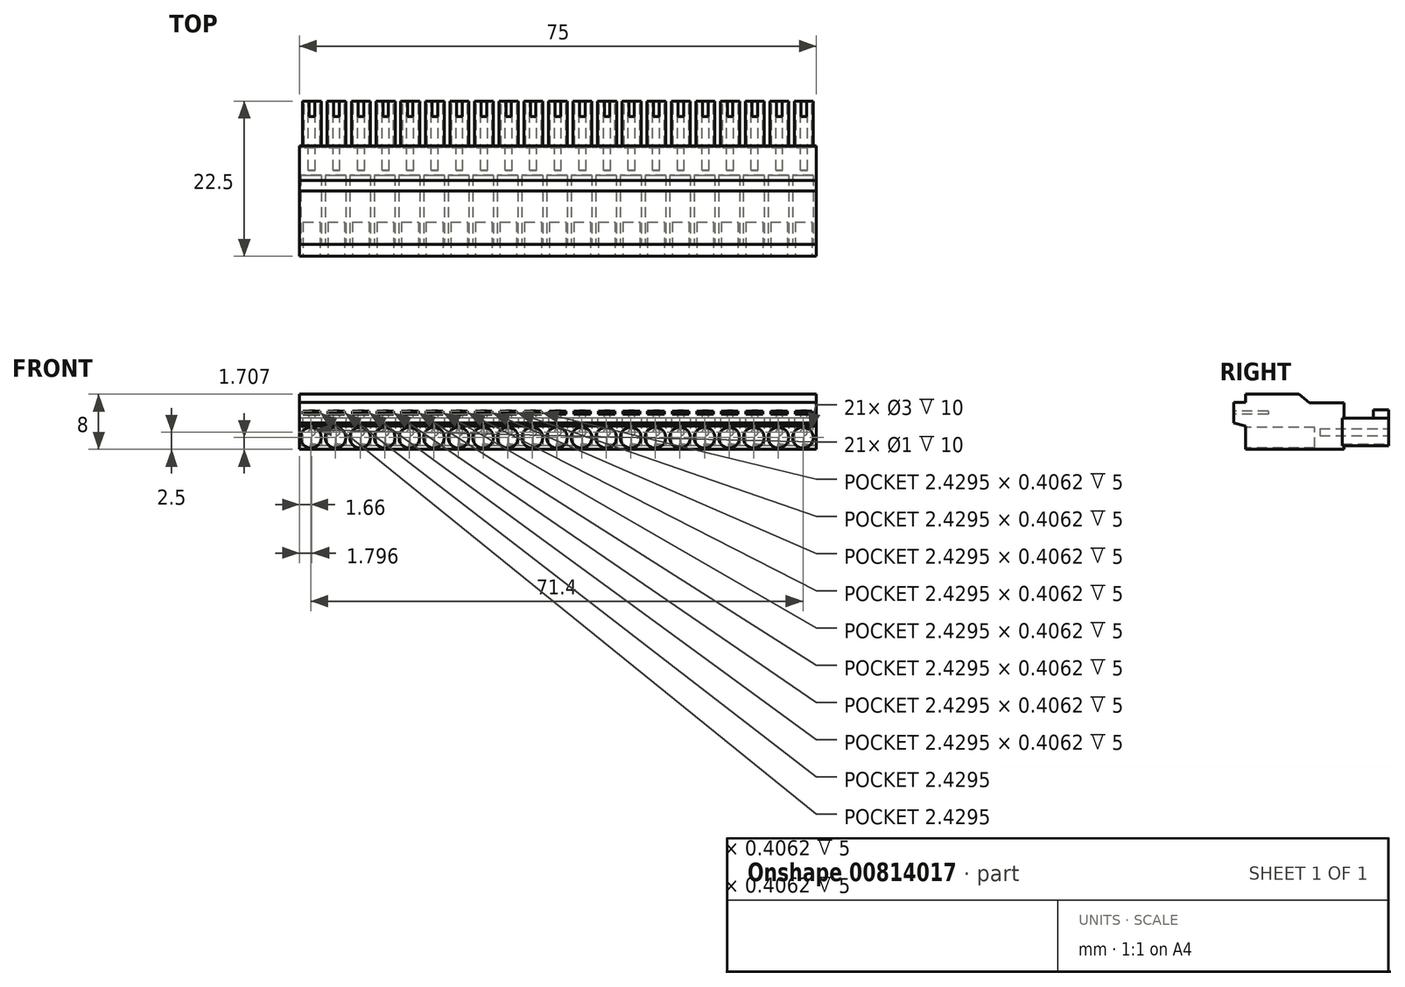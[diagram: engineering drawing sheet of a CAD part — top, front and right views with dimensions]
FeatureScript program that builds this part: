
annotation { "Feature Type Name" : "Feature", "Feature Type Description" : "" }
export const myFeature = defineFeature(function(context is Context, id is Id, definition is map)
    precondition{}
    {
        {
            var Q0;
            Q0=qCreatedBy(makeId("Right.planeOp"),FACE);
            var sketch = newSketch(context, id + "F0", { "sketchPlane" : qUnion([Q0])});
            skLineSegment(sketch, "E0", {"start": v(0, 0) * mm, "end": v(-14.25, 0) * mm});
            skLineSegment(sketch, "E1", {"start": v(-14.25, 0) * mm, "end": v(-14.25, 3.41) * mm});
            skLineSegment(sketch, "E2", {"start": v(-14.25, 8) * mm, "end": v(-6.5, 8) * mm});
            skLineSegment(sketch, "E3", {"start": v(0, 0) * mm, "end": v(0, 6.75) * mm});
            skLineSegment(sketch, "E4", {"start": v(0, 6.75) * mm, "end": v(-5, 6.75) * mm});
            skLineSegment(sketch, "E5", {"start": v(-5, 6.75) * mm, "end": v(-6.5, 8) * mm});
            skPoint(sketch, "E6.orphan", {"position": v(-5, 8) * mm});
            skLineSegment(sketch, "E7", {"start": v(-16, 3.83) * mm, "end": v(-16, 6.83) * mm});
            skLineSegment(sketch, "E8", {"start": v(-16, 6.83) * mm, "end": v(-14.25, 6.83) * mm});
            skLineSegment(sketch, "E9", {"start": v(-16, 3.83) * mm, "end": v(-14.25, 3.41) * mm});
            skLineSegment(sketch, "E10.trimOffspring", {"start": v(-14.25, 6.83) * mm, "end": v(-14.25, 8) * mm});
            skPoint(sketch, "E11.orphan", {"position": v(-14.25, 4) * mm});
            skLineSegment(sketch, "E12", {"start": v(0, 0) * mm, "end": v(0, 0.5) * mm});
            skLineSegment(sketch, "E13", {"start": v(0, 0.5) * mm, "end": v(6.5, 0.5) * mm});
            skLineSegment(sketch, "E14", {"start": v(6.5, 0.5) * mm, "end": v(6.5, 4.5) * mm});
            skLineSegment(sketch, "E15", {"start": v(6.5, 4.5) * mm, "end": v(0, 4.5) * mm});
            skSolve(sketch);
        }
        {
            var Q0;
            Q0=qSketchRegion(id+"F0",true);
            extrude(context, id + "F1", {"entities" : qUnion([Q0]), "depth" : 75 * mm, "offsetDistance" : 25 * mm});
        }
        {
            var Q0;
            Q0=makeQuery(id+"F1.opExtrude","SWEPT_FACE",FACE,{"disambiguationData":[OSD([sQuery(id+"F0.wireOp",EDGE,"E1")])]});
            var sketch = newSketch(context, id + "F2", { "sketchPlane" : qUnion([Q0])});
            skLineSegment(sketch, "E16", {"start": v(0, 1.7) * mm, "end": v(75, 1.7) * mm, "construction": true});
            skCircle(sketch, "E17", {"center": v(1.66, 1.7) * mm, "radius": 1.5 * mm});
            skCircle(sketch, "E18.1.0.0", {"center": v(5.23, 1.7) * mm, "radius": 1.5 * mm});
            skCircle(sketch, "E18.2.0.0", {"center": v(8.8, 1.7) * mm, "radius": 1.5 * mm});
            skCircle(sketch, "E18.3.0.0", {"center": v(12.37, 1.7) * mm, "radius": 1.5 * mm});
            skCircle(sketch, "E18.4.0.0", {"center": v(15.94, 1.7) * mm, "radius": 1.5 * mm});
            skCircle(sketch, "E18.5.0.0", {"center": v(19.51, 1.7) * mm, "radius": 1.5 * mm});
            skCircle(sketch, "E18.6.0.0", {"center": v(23.08, 1.7) * mm, "radius": 1.5 * mm});
            skCircle(sketch, "E18.7.0.0", {"center": v(26.65, 1.7) * mm, "radius": 1.5 * mm});
            skCircle(sketch, "E18.8.0.0", {"center": v(30.22, 1.7) * mm, "radius": 1.5 * mm});
            skCircle(sketch, "E18.9.0.0", {"center": v(33.8, 1.7) * mm, "radius": 1.5 * mm});
            skCircle(sketch, "E18.10.0.0", {"center": v(37.36, 1.7) * mm, "radius": 1.5 * mm});
            skCircle(sketch, "E18.11.0.0", {"center": v(40.93, 1.7) * mm, "radius": 1.5 * mm});
            skCircle(sketch, "E18.12.0.0", {"center": v(44.5, 1.7) * mm, "radius": 1.5 * mm});
            skCircle(sketch, "E18.13.0.0", {"center": v(48.07, 1.7) * mm, "radius": 1.5 * mm});
            skCircle(sketch, "E18.14.0.0", {"center": v(51.64, 1.7) * mm, "radius": 1.5 * mm});
            skCircle(sketch, "E18.15.0.0", {"center": v(55.21, 1.7) * mm, "radius": 1.5 * mm});
            skCircle(sketch, "E18.16.0.0", {"center": v(58.78, 1.7) * mm, "radius": 1.5 * mm});
            skCircle(sketch, "E18.17.0.0", {"center": v(62.35, 1.7) * mm, "radius": 1.5 * mm});
            skCircle(sketch, "E18.18.0.0", {"center": v(65.92, 1.7) * mm, "radius": 1.5 * mm});
            skCircle(sketch, "E18.19.0.0", {"center": v(69.5, 1.7) * mm, "radius": 1.5 * mm});
            skCircle(sketch, "E18.20.0.0", {"center": v(73.06, 1.7) * mm, "radius": 1.5 * mm});
            skLineSegment(sketch, "E18.direction1", {"start": v(1.66, 1.7) * mm, "end": v(5.23, 1.7) * mm, "construction": true});
            skSolve(sketch);
        }
        {
            var Q0;
            Q0=qSketchRegion(id+"F2",true);
            extrude(context, id + "F3", {"entities" : qUnion([Q0]), "operationType" : NewBodyOperationType.REMOVE, "oppositeDirection" : true, "depth" : 10 * mm, "offsetDistance" : 25 * mm});
        }
        {
            var Q0;
            Q0=makeQuery(id+"F1.opExtrude","SWEPT_FACE",FACE,{"disambiguationData":[OSD([sQuery(id+"F0.wireOp",EDGE,"E14")])]});
            var sketch = newSketch(context, id + "F4", { "sketchPlane" : qUnion([Q0])});
            skLineSegment(sketch, "E19", {"start": v(-75, 2.5) * mm, "end": v(0, 2.5) * mm, "construction": true});
            skCircle(sketch, "E20", {"center": v(-73.2, 2.5) * mm, "radius": 0.5 * mm});
            skCircle(sketch, "E21.1.0.0", {"center": v(-69.63, 2.5) * mm, "radius": 0.5 * mm});
            skCircle(sketch, "E21.2.0.0", {"center": v(-66.06, 2.5) * mm, "radius": 0.5 * mm});
            skCircle(sketch, "E21.3.0.0", {"center": v(-62.49, 2.5) * mm, "radius": 0.5 * mm});
            skCircle(sketch, "E21.4.0.0", {"center": v(-58.92, 2.5) * mm, "radius": 0.5 * mm});
            skCircle(sketch, "E21.5.0.0", {"center": v(-55.35, 2.5) * mm, "radius": 0.5 * mm});
            skCircle(sketch, "E21.6.0.0", {"center": v(-51.78, 2.5) * mm, "radius": 0.5 * mm});
            skCircle(sketch, "E21.7.0.0", {"center": v(-48.2, 2.5) * mm, "radius": 0.5 * mm});
            skCircle(sketch, "E21.8.0.0", {"center": v(-44.64, 2.5) * mm, "radius": 0.5 * mm});
            skCircle(sketch, "E21.9.0.0", {"center": v(-41.07, 2.5) * mm, "radius": 0.5 * mm});
            skCircle(sketch, "E21.10.0.0", {"center": v(-37.5, 2.5) * mm, "radius": 0.5 * mm});
            skCircle(sketch, "E21.11.0.0", {"center": v(-33.93, 2.5) * mm, "radius": 0.5 * mm});
            skCircle(sketch, "E21.12.0.0", {"center": v(-30.36, 2.5) * mm, "radius": 0.5 * mm});
            skCircle(sketch, "E21.13.0.0", {"center": v(-26.79, 2.5) * mm, "radius": 0.5 * mm});
            skCircle(sketch, "E21.14.0.0", {"center": v(-23.22, 2.5) * mm, "radius": 0.5 * mm});
            skCircle(sketch, "E21.15.0.0", {"center": v(-19.65, 2.5) * mm, "radius": 0.5 * mm});
            skCircle(sketch, "E21.16.0.0", {"center": v(-16.08, 2.5) * mm, "radius": 0.5 * mm});
            skCircle(sketch, "E21.17.0.0", {"center": v(-12.5, 2.5) * mm, "radius": 0.5 * mm});
            skCircle(sketch, "E21.18.0.0", {"center": v(-8.94, 2.5) * mm, "radius": 0.5 * mm});
            skCircle(sketch, "E21.19.0.0", {"center": v(-5.37, 2.5) * mm, "radius": 0.5 * mm});
            skCircle(sketch, "E21.20.0.0", {"center": v(-1.8, 2.5) * mm, "radius": 0.5 * mm});
            skLineSegment(sketch, "E21.direction1", {"start": v(-73.2, 2.5) * mm, "end": v(-69.63, 2.5) * mm, "construction": true});
            skSolve(sketch);
        }
        {
            var Q0;
            Q0=qSketchRegion(id+"F4",true);
            extrude(context, id + "F5", {"entities" : qUnion([Q0]), "operationType" : NewBodyOperationType.REMOVE, "oppositeDirection" : true, "depth" : 10 * mm, "offsetDistance" : 25 * mm});
        }
        {
            var Q0;
            Q0=makeQuery(id+"F1.opExtrude","SWEPT_FACE",FACE,{"disambiguationData":[OSD([sQuery(id+"F0.wireOp",EDGE,"E14")])]});
            var sketch = newSketch(context, id + "F6", { "sketchPlane" : qUnion([Q0])});
            skLineSegment(sketch, "E22", {"start": v(-73.2, 2.5) * mm, "end": v(-73.2, 5.96) * mm, "construction": true});
            skLineSegment(sketch, "E23", {"start": v(-73.2, 5.96) * mm, "end": v(-73.2, 0.5) * mm, "construction": true});
            skLineSegment(sketch, "E24.left", {"start": v(-71.82, 4.5) * mm, "end": v(-71.82, 0.5) * mm});
            skPoint(sketch, "E24.middle", {"position": v(-73.2, 2.5) * mm});
            skArc(sketch, "E25", {"start": v(-72.09, 0.5) * mm, "mid": v(-73.23, 0.75) * mm, "end": v(-74.37, 0.5) * mm});
            skLineSegment(sketch, "E26.right", {"start": v(-71, 4.5) * mm, "end": v(-71, 0.5) * mm});
            skPoint(sketch, "E26.middle", {"position": v(-69.63, 2.5) * mm});
            skLineSegment(sketch, "E27.bottom", {"start": v(-71.82, 4.5) * mm, "end": v(-71, 4.5) * mm});
            skLineSegment(sketch, "E27.top", {"start": v(-71.82, 0.5) * mm, "end": v(-71, 0.5) * mm});
            skLineSegment(sketch, "E28", {"start": v(-74.37, 0.5) * mm, "end": v(-72.09, 0.5) * mm});
            skPoint(sketch, "E24.right.end.orphan", {"position": v(-74.57, 0.5) * mm});
            skPoint(sketch, "E24.bottom.end.orphan", {"position": v(-74.57, 4.5) * mm});
            skPoint(sketch, "E26.left.start.orphan", {"position": v(-68.25, 4.5) * mm});
            skPoint(sketch, "E26.top.start.orphan", {"position": v(-68.25, 0.5) * mm});
            skLineSegment(sketch, "E29.1.0.0", {"start": v(-67.43, 4.5) * mm, "end": v(-67.43, 0.5) * mm});
            skLineSegment(sketch, "E29.1.0.1", {"start": v(-68.25, 4.5) * mm, "end": v(-67.43, 4.5) * mm});
            skLineSegment(sketch, "E29.1.0.2", {"start": v(-68.25, 4.5) * mm, "end": v(-68.25, 0.5) * mm});
            skLineSegment(sketch, "E29.1.0.3", {"start": v(-68.25, 0.5) * mm, "end": v(-67.43, 0.5) * mm});
            skLineSegment(sketch, "E29.1.0.4", {"start": v(-67.43, 4.5) * mm, "end": v(-67.43, 0.5) * mm});
            skLineSegment(sketch, "E29.1.0.5", {"start": v(-68.25, 4.5) * mm, "end": v(-68.25, 0.5) * mm});
            skArc(sketch, "E29.1.0.6", {"start": v(-68.52, 0.5) * mm, "mid": v(-69.66, 0.75) * mm, "end": v(-70.8, 0.5) * mm});
            skLineSegment(sketch, "E29.1.0.7", {"start": v(-70.8, 0.5) * mm, "end": v(-68.52, 0.5) * mm});
            skLineSegment(sketch, "E29.2.0.0", {"start": v(-63.86, 4.5) * mm, "end": v(-63.86, 0.5) * mm});
            skLineSegment(sketch, "E29.2.0.1", {"start": v(-64.68, 4.5) * mm, "end": v(-63.86, 4.5) * mm});
            skLineSegment(sketch, "E29.2.0.2", {"start": v(-64.68, 4.5) * mm, "end": v(-64.68, 0.5) * mm});
            skLineSegment(sketch, "E29.2.0.3", {"start": v(-64.68, 0.5) * mm, "end": v(-63.86, 0.5) * mm});
            skLineSegment(sketch, "E29.2.0.4", {"start": v(-63.86, 4.5) * mm, "end": v(-63.86, 0.5) * mm});
            skLineSegment(sketch, "E29.2.0.5", {"start": v(-64.68, 4.5) * mm, "end": v(-64.68, 0.5) * mm});
            skArc(sketch, "E29.2.0.6", {"start": v(-64.95, 0.5) * mm, "mid": v(-66.09, 0.75) * mm, "end": v(-67.23, 0.5) * mm});
            skLineSegment(sketch, "E29.2.0.7", {"start": v(-67.23, 0.5) * mm, "end": v(-64.95, 0.5) * mm});
            skLineSegment(sketch, "E29.3.0.0", {"start": v(-60.3, 4.5) * mm, "end": v(-60.3, 0.5) * mm});
            skLineSegment(sketch, "E29.3.0.1", {"start": v(-61.11, 4.5) * mm, "end": v(-60.3, 4.5) * mm});
            skLineSegment(sketch, "E29.3.0.2", {"start": v(-61.11, 4.5) * mm, "end": v(-61.11, 0.5) * mm});
            skLineSegment(sketch, "E29.3.0.3", {"start": v(-61.11, 0.5) * mm, "end": v(-60.3, 0.5) * mm});
            skLineSegment(sketch, "E29.3.0.4", {"start": v(-60.3, 4.5) * mm, "end": v(-60.3, 0.5) * mm});
            skLineSegment(sketch, "E29.3.0.5", {"start": v(-61.11, 4.5) * mm, "end": v(-61.11, 0.5) * mm});
            skArc(sketch, "E29.3.0.6", {"start": v(-61.38, 0.5) * mm, "mid": v(-62.52, 0.75) * mm, "end": v(-63.66, 0.5) * mm});
            skLineSegment(sketch, "E29.3.0.7", {"start": v(-63.66, 0.5) * mm, "end": v(-61.38, 0.5) * mm});
            skLineSegment(sketch, "E29.4.0.0", {"start": v(-56.72, 4.5) * mm, "end": v(-56.72, 0.5) * mm});
            skLineSegment(sketch, "E29.4.0.1", {"start": v(-57.54, 4.5) * mm, "end": v(-56.72, 4.5) * mm});
            skLineSegment(sketch, "E29.4.0.2", {"start": v(-57.54, 4.5) * mm, "end": v(-57.54, 0.5) * mm});
            skLineSegment(sketch, "E29.4.0.3", {"start": v(-57.54, 0.5) * mm, "end": v(-56.72, 0.5) * mm});
            skLineSegment(sketch, "E29.4.0.4", {"start": v(-56.72, 4.5) * mm, "end": v(-56.72, 0.5) * mm});
            skLineSegment(sketch, "E29.4.0.5", {"start": v(-57.54, 4.5) * mm, "end": v(-57.54, 0.5) * mm});
            skArc(sketch, "E29.4.0.6", {"start": v(-57.8, 0.5) * mm, "mid": v(-58.95, 0.75) * mm, "end": v(-60.1, 0.5) * mm});
            skLineSegment(sketch, "E29.4.0.7", {"start": v(-60.1, 0.5) * mm, "end": v(-57.8, 0.5) * mm});
            skLineSegment(sketch, "E29.5.0.0", {"start": v(-53.15, 4.5) * mm, "end": v(-53.15, 0.5) * mm});
            skLineSegment(sketch, "E29.5.0.1", {"start": v(-53.97, 4.5) * mm, "end": v(-53.15, 4.5) * mm});
            skLineSegment(sketch, "E29.5.0.2", {"start": v(-53.97, 4.5) * mm, "end": v(-53.97, 0.5) * mm});
            skLineSegment(sketch, "E29.5.0.3", {"start": v(-53.97, 0.5) * mm, "end": v(-53.15, 0.5) * mm});
            skLineSegment(sketch, "E29.5.0.4", {"start": v(-53.15, 4.5) * mm, "end": v(-53.15, 0.5) * mm});
            skLineSegment(sketch, "E29.5.0.5", {"start": v(-53.97, 4.5) * mm, "end": v(-53.97, 0.5) * mm});
            skArc(sketch, "E29.5.0.6", {"start": v(-54.24, 0.5) * mm, "mid": v(-55.38, 0.75) * mm, "end": v(-56.52, 0.5) * mm});
            skLineSegment(sketch, "E29.5.0.7", {"start": v(-56.52, 0.5) * mm, "end": v(-54.24, 0.5) * mm});
            skLineSegment(sketch, "E29.6.0.0", {"start": v(-49.58, 4.5) * mm, "end": v(-49.58, 0.5) * mm});
            skLineSegment(sketch, "E29.6.0.1", {"start": v(-50.4, 4.5) * mm, "end": v(-49.58, 4.5) * mm});
            skLineSegment(sketch, "E29.6.0.2", {"start": v(-50.4, 4.5) * mm, "end": v(-50.4, 0.5) * mm});
            skLineSegment(sketch, "E29.6.0.3", {"start": v(-50.4, 0.5) * mm, "end": v(-49.58, 0.5) * mm});
            skLineSegment(sketch, "E29.6.0.4", {"start": v(-49.58, 4.5) * mm, "end": v(-49.58, 0.5) * mm});
            skLineSegment(sketch, "E29.6.0.5", {"start": v(-50.4, 4.5) * mm, "end": v(-50.4, 0.5) * mm});
            skArc(sketch, "E29.6.0.6", {"start": v(-50.67, 0.5) * mm, "mid": v(-51.8, 0.75) * mm, "end": v(-52.95, 0.5) * mm});
            skLineSegment(sketch, "E29.6.0.7", {"start": v(-52.95, 0.5) * mm, "end": v(-50.67, 0.5) * mm});
            skLineSegment(sketch, "E29.7.0.0", {"start": v(-46.01, 4.5) * mm, "end": v(-46.01, 0.5) * mm});
            skLineSegment(sketch, "E29.7.0.1", {"start": v(-46.83, 4.5) * mm, "end": v(-46.01, 4.5) * mm});
            skLineSegment(sketch, "E29.7.0.2", {"start": v(-46.83, 4.5) * mm, "end": v(-46.83, 0.5) * mm});
            skLineSegment(sketch, "E29.7.0.3", {"start": v(-46.83, 0.5) * mm, "end": v(-46.01, 0.5) * mm});
            skLineSegment(sketch, "E29.7.0.4", {"start": v(-46.01, 4.5) * mm, "end": v(-46.01, 0.5) * mm});
            skLineSegment(sketch, "E29.7.0.5", {"start": v(-46.83, 4.5) * mm, "end": v(-46.83, 0.5) * mm});
            skArc(sketch, "E29.7.0.6", {"start": v(-47.1, 0.5) * mm, "mid": v(-48.24, 0.75) * mm, "end": v(-49.38, 0.5) * mm});
            skLineSegment(sketch, "E29.7.0.7", {"start": v(-49.38, 0.5) * mm, "end": v(-47.1, 0.5) * mm});
            skLineSegment(sketch, "E29.8.0.0", {"start": v(-42.44, 4.5) * mm, "end": v(-42.44, 0.5) * mm});
            skLineSegment(sketch, "E29.8.0.1", {"start": v(-43.26, 4.5) * mm, "end": v(-42.44, 4.5) * mm});
            skLineSegment(sketch, "E29.8.0.2", {"start": v(-43.26, 4.5) * mm, "end": v(-43.26, 0.5) * mm});
            skLineSegment(sketch, "E29.8.0.3", {"start": v(-43.26, 0.5) * mm, "end": v(-42.44, 0.5) * mm});
            skLineSegment(sketch, "E29.8.0.4", {"start": v(-42.44, 4.5) * mm, "end": v(-42.44, 0.5) * mm});
            skLineSegment(sketch, "E29.8.0.5", {"start": v(-43.26, 4.5) * mm, "end": v(-43.26, 0.5) * mm});
            skArc(sketch, "E29.8.0.6", {"start": v(-43.53, 0.5) * mm, "mid": v(-44.67, 0.75) * mm, "end": v(-45.81, 0.5) * mm});
            skLineSegment(sketch, "E29.8.0.7", {"start": v(-45.81, 0.5) * mm, "end": v(-43.53, 0.5) * mm});
            skLineSegment(sketch, "E29.9.0.0", {"start": v(-38.87, 4.5) * mm, "end": v(-38.87, 0.5) * mm});
            skLineSegment(sketch, "E29.9.0.1", {"start": v(-39.7, 4.5) * mm, "end": v(-38.87, 4.5) * mm});
            skLineSegment(sketch, "E29.9.0.2", {"start": v(-39.7, 4.5) * mm, "end": v(-39.7, 0.5) * mm});
            skLineSegment(sketch, "E29.9.0.3", {"start": v(-39.7, 0.5) * mm, "end": v(-38.87, 0.5) * mm});
            skLineSegment(sketch, "E29.9.0.4", {"start": v(-38.87, 4.5) * mm, "end": v(-38.87, 0.5) * mm});
            skLineSegment(sketch, "E29.9.0.5", {"start": v(-39.7, 4.5) * mm, "end": v(-39.7, 0.5) * mm});
            skArc(sketch, "E29.9.0.6", {"start": v(-39.96, 0.5) * mm, "mid": v(-41.1, 0.75) * mm, "end": v(-42.24, 0.5) * mm});
            skLineSegment(sketch, "E29.9.0.7", {"start": v(-42.24, 0.5) * mm, "end": v(-39.96, 0.5) * mm});
            skLineSegment(sketch, "E29.10.0.0", {"start": v(-35.3, 4.5) * mm, "end": v(-35.3, 0.5) * mm});
            skLineSegment(sketch, "E29.10.0.1", {"start": v(-36.12, 4.5) * mm, "end": v(-35.3, 4.5) * mm});
            skLineSegment(sketch, "E29.10.0.2", {"start": v(-36.12, 4.5) * mm, "end": v(-36.12, 0.5) * mm});
            skLineSegment(sketch, "E29.10.0.3", {"start": v(-36.12, 0.5) * mm, "end": v(-35.3, 0.5) * mm});
            skLineSegment(sketch, "E29.10.0.4", {"start": v(-35.3, 4.5) * mm, "end": v(-35.3, 0.5) * mm});
            skLineSegment(sketch, "E29.10.0.5", {"start": v(-36.12, 4.5) * mm, "end": v(-36.12, 0.5) * mm});
            skArc(sketch, "E29.10.0.6", {"start": v(-36.39, 0.5) * mm, "mid": v(-37.53, 0.75) * mm, "end": v(-38.67, 0.5) * mm});
            skLineSegment(sketch, "E29.10.0.7", {"start": v(-38.67, 0.5) * mm, "end": v(-36.39, 0.5) * mm});
            skLineSegment(sketch, "E29.11.0.0", {"start": v(-31.73, 4.5) * mm, "end": v(-31.73, 0.5) * mm});
            skLineSegment(sketch, "E29.11.0.1", {"start": v(-32.55, 4.5) * mm, "end": v(-31.73, 4.5) * mm});
            skLineSegment(sketch, "E29.11.0.2", {"start": v(-32.55, 4.5) * mm, "end": v(-32.55, 0.5) * mm});
            skLineSegment(sketch, "E29.11.0.3", {"start": v(-32.55, 0.5) * mm, "end": v(-31.73, 0.5) * mm});
            skLineSegment(sketch, "E29.11.0.4", {"start": v(-31.73, 4.5) * mm, "end": v(-31.73, 0.5) * mm});
            skLineSegment(sketch, "E29.11.0.5", {"start": v(-32.55, 4.5) * mm, "end": v(-32.55, 0.5) * mm});
            skArc(sketch, "E29.11.0.6", {"start": v(-32.82, 0.5) * mm, "mid": v(-33.96, 0.75) * mm, "end": v(-35.1, 0.5) * mm});
            skLineSegment(sketch, "E29.11.0.7", {"start": v(-35.1, 0.5) * mm, "end": v(-32.82, 0.5) * mm});
            skLineSegment(sketch, "E29.12.0.0", {"start": v(-28.16, 4.5) * mm, "end": v(-28.16, 0.5) * mm});
            skLineSegment(sketch, "E29.12.0.1", {"start": v(-28.98, 4.5) * mm, "end": v(-28.16, 4.5) * mm});
            skLineSegment(sketch, "E29.12.0.2", {"start": v(-28.98, 4.5) * mm, "end": v(-28.98, 0.5) * mm});
            skLineSegment(sketch, "E29.12.0.3", {"start": v(-28.98, 0.5) * mm, "end": v(-28.16, 0.5) * mm});
            skLineSegment(sketch, "E29.12.0.4", {"start": v(-28.16, 4.5) * mm, "end": v(-28.16, 0.5) * mm});
            skLineSegment(sketch, "E29.12.0.5", {"start": v(-28.98, 4.5) * mm, "end": v(-28.98, 0.5) * mm});
            skArc(sketch, "E29.12.0.6", {"start": v(-29.25, 0.5) * mm, "mid": v(-30.39, 0.75) * mm, "end": v(-31.53, 0.5) * mm});
            skLineSegment(sketch, "E29.12.0.7", {"start": v(-31.53, 0.5) * mm, "end": v(-29.25, 0.5) * mm});
            skLineSegment(sketch, "E29.13.0.0", {"start": v(-24.6, 4.5) * mm, "end": v(-24.6, 0.5) * mm});
            skLineSegment(sketch, "E29.13.0.1", {"start": v(-25.41, 4.5) * mm, "end": v(-24.6, 4.5) * mm});
            skLineSegment(sketch, "E29.13.0.2", {"start": v(-25.41, 4.5) * mm, "end": v(-25.41, 0.5) * mm});
            skLineSegment(sketch, "E29.13.0.3", {"start": v(-25.41, 0.5) * mm, "end": v(-24.6, 0.5) * mm});
            skLineSegment(sketch, "E29.13.0.4", {"start": v(-24.6, 4.5) * mm, "end": v(-24.6, 0.5) * mm});
            skLineSegment(sketch, "E29.13.0.5", {"start": v(-25.41, 4.5) * mm, "end": v(-25.41, 0.5) * mm});
            skArc(sketch, "E29.13.0.6", {"start": v(-25.68, 0.5) * mm, "mid": v(-26.82, 0.75) * mm, "end": v(-27.96, 0.5) * mm});
            skLineSegment(sketch, "E29.13.0.7", {"start": v(-27.96, 0.5) * mm, "end": v(-25.68, 0.5) * mm});
            skLineSegment(sketch, "E29.14.0.0", {"start": v(-21.02, 4.5) * mm, "end": v(-21.02, 0.5) * mm});
            skLineSegment(sketch, "E29.14.0.1", {"start": v(-21.84, 4.5) * mm, "end": v(-21.02, 4.5) * mm});
            skLineSegment(sketch, "E29.14.0.2", {"start": v(-21.84, 4.5) * mm, "end": v(-21.84, 0.5) * mm});
            skLineSegment(sketch, "E29.14.0.3", {"start": v(-21.84, 0.5) * mm, "end": v(-21.02, 0.5) * mm});
            skLineSegment(sketch, "E29.14.0.4", {"start": v(-21.02, 4.5) * mm, "end": v(-21.02, 0.5) * mm});
            skLineSegment(sketch, "E29.14.0.5", {"start": v(-21.84, 4.5) * mm, "end": v(-21.84, 0.5) * mm});
            skArc(sketch, "E29.14.0.6", {"start": v(-22.1, 0.5) * mm, "mid": v(-23.25, 0.75) * mm, "end": v(-24.4, 0.5) * mm});
            skLineSegment(sketch, "E29.14.0.7", {"start": v(-24.4, 0.5) * mm, "end": v(-22.1, 0.5) * mm});
            skLineSegment(sketch, "E29.15.0.0", {"start": v(-17.45, 4.5) * mm, "end": v(-17.45, 0.5) * mm});
            skLineSegment(sketch, "E29.15.0.1", {"start": v(-18.27, 4.5) * mm, "end": v(-17.45, 4.5) * mm});
            skLineSegment(sketch, "E29.15.0.2", {"start": v(-18.27, 4.5) * mm, "end": v(-18.27, 0.5) * mm});
            skLineSegment(sketch, "E29.15.0.3", {"start": v(-18.27, 0.5) * mm, "end": v(-17.45, 0.5) * mm});
            skLineSegment(sketch, "E29.15.0.4", {"start": v(-17.45, 4.5) * mm, "end": v(-17.45, 0.5) * mm});
            skLineSegment(sketch, "E29.15.0.5", {"start": v(-18.27, 4.5) * mm, "end": v(-18.27, 0.5) * mm});
            skArc(sketch, "E29.15.0.6", {"start": v(-18.54, 0.5) * mm, "mid": v(-19.68, 0.75) * mm, "end": v(-20.82, 0.5) * mm});
            skLineSegment(sketch, "E29.15.0.7", {"start": v(-20.82, 0.5) * mm, "end": v(-18.54, 0.5) * mm});
            skLineSegment(sketch, "E29.16.0.0", {"start": v(-13.88, 4.5) * mm, "end": v(-13.88, 0.5) * mm});
            skLineSegment(sketch, "E29.16.0.1", {"start": v(-14.7, 4.5) * mm, "end": v(-13.88, 4.5) * mm});
            skLineSegment(sketch, "E29.16.0.2", {"start": v(-14.7, 4.5) * mm, "end": v(-14.7, 0.5) * mm});
            skLineSegment(sketch, "E29.16.0.3", {"start": v(-14.7, 0.5) * mm, "end": v(-13.88, 0.5) * mm});
            skLineSegment(sketch, "E29.16.0.4", {"start": v(-13.88, 4.5) * mm, "end": v(-13.88, 0.5) * mm});
            skLineSegment(sketch, "E29.16.0.5", {"start": v(-14.7, 4.5) * mm, "end": v(-14.7, 0.5) * mm});
            skArc(sketch, "E29.16.0.6", {"start": v(-14.97, 0.5) * mm, "mid": v(-16.1, 0.75) * mm, "end": v(-17.25, 0.5) * mm});
            skLineSegment(sketch, "E29.16.0.7", {"start": v(-17.25, 0.5) * mm, "end": v(-14.97, 0.5) * mm});
            skLineSegment(sketch, "E29.17.0.0", {"start": v(-10.31, 4.5) * mm, "end": v(-10.31, 0.5) * mm});
            skLineSegment(sketch, "E29.17.0.1", {"start": v(-11.13, 4.5) * mm, "end": v(-10.31, 4.5) * mm});
            skLineSegment(sketch, "E29.17.0.2", {"start": v(-11.13, 4.5) * mm, "end": v(-11.13, 0.5) * mm});
            skLineSegment(sketch, "E29.17.0.3", {"start": v(-11.13, 0.5) * mm, "end": v(-10.31, 0.5) * mm});
            skLineSegment(sketch, "E29.17.0.4", {"start": v(-10.31, 4.5) * mm, "end": v(-10.31, 0.5) * mm});
            skLineSegment(sketch, "E29.17.0.5", {"start": v(-11.13, 4.5) * mm, "end": v(-11.13, 0.5) * mm});
            skArc(sketch, "E29.17.0.6", {"start": v(-11.4, 0.5) * mm, "mid": v(-12.54, 0.75) * mm, "end": v(-13.68, 0.5) * mm});
            skLineSegment(sketch, "E29.17.0.7", {"start": v(-13.68, 0.5) * mm, "end": v(-11.4, 0.5) * mm});
            skLineSegment(sketch, "E29.18.0.0", {"start": v(-6.74, 4.5) * mm, "end": v(-6.74, 0.5) * mm});
            skLineSegment(sketch, "E29.18.0.1", {"start": v(-7.56, 4.5) * mm, "end": v(-6.74, 4.5) * mm});
            skLineSegment(sketch, "E29.18.0.2", {"start": v(-7.56, 4.5) * mm, "end": v(-7.56, 0.5) * mm});
            skLineSegment(sketch, "E29.18.0.3", {"start": v(-7.56, 0.5) * mm, "end": v(-6.74, 0.5) * mm});
            skLineSegment(sketch, "E29.18.0.4", {"start": v(-6.74, 4.5) * mm, "end": v(-6.74, 0.5) * mm});
            skLineSegment(sketch, "E29.18.0.5", {"start": v(-7.56, 4.5) * mm, "end": v(-7.56, 0.5) * mm});
            skArc(sketch, "E29.18.0.6", {"start": v(-7.83, 0.5) * mm, "mid": v(-8.97, 0.75) * mm, "end": v(-10.11, 0.5) * mm});
            skLineSegment(sketch, "E29.18.0.7", {"start": v(-10.11, 0.5) * mm, "end": v(-7.83, 0.5) * mm});
            skLineSegment(sketch, "E29.19.0.0", {"start": v(-3.17, 4.5) * mm, "end": v(-3.17, 0.5) * mm});
            skLineSegment(sketch, "E29.19.0.1", {"start": v(-4, 4.5) * mm, "end": v(-3.17, 4.5) * mm});
            skLineSegment(sketch, "E29.19.0.2", {"start": v(-4, 4.5) * mm, "end": v(-4, 0.5) * mm});
            skLineSegment(sketch, "E29.19.0.3", {"start": v(-4, 0.5) * mm, "end": v(-3.17, 0.5) * mm});
            skLineSegment(sketch, "E29.19.0.4", {"start": v(-3.17, 4.5) * mm, "end": v(-3.17, 0.5) * mm});
            skLineSegment(sketch, "E29.19.0.5", {"start": v(-4, 4.5) * mm, "end": v(-4, 0.5) * mm});
            skArc(sketch, "E29.19.0.6", {"start": v(-4.26, 0.5) * mm, "mid": v(-5.4, 0.75) * mm, "end": v(-6.54, 0.5) * mm});
            skLineSegment(sketch, "E29.19.0.7", {"start": v(-6.54, 0.5) * mm, "end": v(-4.26, 0.5) * mm});
            skLineSegment(sketch, "E29.20.0.0", {"start": v(0.4, 4.5) * mm, "end": v(0.4, 0.5) * mm});
            skLineSegment(sketch, "E29.20.0.1", {"start": v(-0.42, 4.5) * mm, "end": v(0.4, 4.5) * mm});
            skLineSegment(sketch, "E29.20.0.2", {"start": v(-0.42, 4.5) * mm, "end": v(-0.42, 0.5) * mm});
            skLineSegment(sketch, "E29.20.0.3", {"start": v(-0.42, 0.5) * mm, "end": v(0.4, 0.5) * mm});
            skLineSegment(sketch, "E29.20.0.4", {"start": v(0.4, 4.5) * mm, "end": v(0.4, 0.5) * mm});
            skLineSegment(sketch, "E29.20.0.5", {"start": v(-0.42, 4.5) * mm, "end": v(-0.42, 0.5) * mm});
            skArc(sketch, "E29.20.0.6", {"start": v(-0.69, 0.5) * mm, "mid": v(-1.83, 0.75) * mm, "end": v(-2.97, 0.5) * mm});
            skLineSegment(sketch, "E29.20.0.7", {"start": v(-2.97, 0.5) * mm, "end": v(-0.69, 0.5) * mm});
            skLineSegment(sketch, "E29.direction1", {"start": v(-71.82, 0.5) * mm, "end": v(-68.25, 0.5) * mm, "construction": true});
            skLineSegment(sketch, "E30.bottom", {"start": v(-74.57, 0.5) * mm, "end": v(-75, 0.5) * mm});
            skLineSegment(sketch, "E30.top", {"start": v(-74.57, 4.5) * mm, "end": v(-75, 4.5) * mm});
            skLineSegment(sketch, "E30.left", {"start": v(-74.57, 0.5) * mm, "end": v(-74.57, 4.5) * mm});
            skLineSegment(sketch, "E30.right", {"start": v(-75, 0.5) * mm, "end": v(-75, 4.5) * mm});
            skSolve(sketch);
        }
        {
            var Q0;
            Q0=qSketchRegion(id+"F6",true);
            extrude(context, id + "F7", {"entities" : qUnion([Q0]), "operationType" : NewBodyOperationType.REMOVE, "oppositeDirection" : true, "depth" : 6.75 * mm, "offsetDistance" : 25 * mm});
        }
        {
            var Q0;
            Q0=makeQuery(id+"F7.boolean.opBoolean","SPLIT",FACE,{"disambiguationData":[TD([makeQuery(id+"F5.boolean.opBoolean","COPY",FACE,{"derivedFrom":makeQuery(id+"F5.opExtrude","SWEPT_FACE",FACE,{"disambiguationData":[OSD([sQuery(id+"F4.wireOp",EDGE,"E20")])]})})])],"derivedFrom":makeQuery(id+"F1.opExtrude","SWEPT_FACE",FACE,{"disambiguationData":[OSD([sQuery(id+"F0.wireOp",EDGE,"E14")])]})});
            var sketch = newSketch(context, id + "F8", { "sketchPlane" : qUnion([Q0])});
            skLineSegment(sketch, "E31", {"start": v(-73.2, 2.5) * mm, "end": v(-73.2, 4.5) * mm, "construction": true});
            skLineSegment(sketch, "E32", {"start": v(-73.2, 4.5) * mm, "end": v(-73.2, 5.75) * mm, "construction": true});
            skLineSegment(sketch, "E33", {"start": v(-73.2, 5.75) * mm, "end": v(-73.6, 5.75) * mm});
            skLineSegment(sketch, "E34", {"start": v(-73.6, 5.75) * mm, "end": v(-73.6, 4.5) * mm});
            skLineSegment(sketch, "E35", {"start": v(-73.6, 4.5) * mm, "end": v(-72.8, 4.5) * mm});
            skLineSegment(sketch, "E36", {"start": v(-72.8, 4.5) * mm, "end": v(-72.8, 5.75) * mm});
            skLineSegment(sketch, "E37", {"start": v(-72.8, 5.75) * mm, "end": v(-73.2, 5.75) * mm});
            skLineSegment(sketch, "E38.1.0.0", {"start": v(-69.23, 5.75) * mm, "end": v(-69.63, 5.75) * mm});
            skLineSegment(sketch, "E38.1.0.1", {"start": v(-69.63, 5.75) * mm, "end": v(-70.03, 5.75) * mm});
            skLineSegment(sketch, "E38.1.0.2", {"start": v(-70.03, 5.75) * mm, "end": v(-70.03, 4.5) * mm});
            skLineSegment(sketch, "E38.1.0.3", {"start": v(-69.23, 4.5) * mm, "end": v(-69.23, 5.75) * mm});
            skLineSegment(sketch, "E38.1.0.4", {"start": v(-70.03, 4.5) * mm, "end": v(-69.23, 4.5) * mm});
            skLineSegment(sketch, "E38.2.0.0", {"start": v(-65.66, 5.75) * mm, "end": v(-66.06, 5.75) * mm});
            skLineSegment(sketch, "E38.2.0.1", {"start": v(-66.06, 5.75) * mm, "end": v(-66.46, 5.75) * mm});
            skLineSegment(sketch, "E38.2.0.2", {"start": v(-66.46, 5.75) * mm, "end": v(-66.46, 4.5) * mm});
            skLineSegment(sketch, "E38.2.0.3", {"start": v(-65.66, 4.5) * mm, "end": v(-65.66, 5.75) * mm});
            skLineSegment(sketch, "E38.2.0.4", {"start": v(-66.46, 4.5) * mm, "end": v(-65.66, 4.5) * mm});
            skLineSegment(sketch, "E38.3.0.0", {"start": v(-62.09, 5.75) * mm, "end": v(-62.49, 5.75) * mm});
            skLineSegment(sketch, "E38.3.0.1", {"start": v(-62.49, 5.75) * mm, "end": v(-62.89, 5.75) * mm});
            skLineSegment(sketch, "E38.3.0.2", {"start": v(-62.89, 5.75) * mm, "end": v(-62.89, 4.5) * mm});
            skLineSegment(sketch, "E38.3.0.3", {"start": v(-62.09, 4.5) * mm, "end": v(-62.09, 5.75) * mm});
            skLineSegment(sketch, "E38.3.0.4", {"start": v(-62.89, 4.5) * mm, "end": v(-62.09, 4.5) * mm});
            skLineSegment(sketch, "E38.4.0.0", {"start": v(-58.52, 5.75) * mm, "end": v(-58.92, 5.75) * mm});
            skLineSegment(sketch, "E38.4.0.1", {"start": v(-58.92, 5.75) * mm, "end": v(-59.32, 5.75) * mm});
            skLineSegment(sketch, "E38.4.0.2", {"start": v(-59.32, 5.75) * mm, "end": v(-59.32, 4.5) * mm});
            skLineSegment(sketch, "E38.4.0.3", {"start": v(-58.52, 4.5) * mm, "end": v(-58.52, 5.75) * mm});
            skLineSegment(sketch, "E38.4.0.4", {"start": v(-59.32, 4.5) * mm, "end": v(-58.52, 4.5) * mm});
            skLineSegment(sketch, "E38.5.0.0", {"start": v(-54.95, 5.75) * mm, "end": v(-55.35, 5.75) * mm});
            skLineSegment(sketch, "E38.5.0.1", {"start": v(-55.35, 5.75) * mm, "end": v(-55.75, 5.75) * mm});
            skLineSegment(sketch, "E38.5.0.2", {"start": v(-55.75, 5.75) * mm, "end": v(-55.75, 4.5) * mm});
            skLineSegment(sketch, "E38.5.0.3", {"start": v(-54.95, 4.5) * mm, "end": v(-54.95, 5.75) * mm});
            skLineSegment(sketch, "E38.5.0.4", {"start": v(-55.75, 4.5) * mm, "end": v(-54.95, 4.5) * mm});
            skLineSegment(sketch, "E38.6.0.0", {"start": v(-51.38, 5.75) * mm, "end": v(-51.78, 5.75) * mm});
            skLineSegment(sketch, "E38.6.0.1", {"start": v(-51.78, 5.75) * mm, "end": v(-52.18, 5.75) * mm});
            skLineSegment(sketch, "E38.6.0.2", {"start": v(-52.18, 5.75) * mm, "end": v(-52.18, 4.5) * mm});
            skLineSegment(sketch, "E38.6.0.3", {"start": v(-51.38, 4.5) * mm, "end": v(-51.38, 5.75) * mm});
            skLineSegment(sketch, "E38.6.0.4", {"start": v(-52.18, 4.5) * mm, "end": v(-51.38, 4.5) * mm});
            skLineSegment(sketch, "E38.7.0.0", {"start": v(-47.8, 5.75) * mm, "end": v(-48.2, 5.75) * mm});
            skLineSegment(sketch, "E38.7.0.1", {"start": v(-48.2, 5.75) * mm, "end": v(-48.6, 5.75) * mm});
            skLineSegment(sketch, "E38.7.0.2", {"start": v(-48.6, 5.75) * mm, "end": v(-48.6, 4.5) * mm});
            skLineSegment(sketch, "E38.7.0.3", {"start": v(-47.8, 4.5) * mm, "end": v(-47.8, 5.75) * mm});
            skLineSegment(sketch, "E38.7.0.4", {"start": v(-48.6, 4.5) * mm, "end": v(-47.8, 4.5) * mm});
            skLineSegment(sketch, "E38.8.0.0", {"start": v(-44.24, 5.75) * mm, "end": v(-44.64, 5.75) * mm});
            skLineSegment(sketch, "E38.8.0.1", {"start": v(-44.64, 5.75) * mm, "end": v(-45.04, 5.75) * mm});
            skLineSegment(sketch, "E38.8.0.2", {"start": v(-45.04, 5.75) * mm, "end": v(-45.04, 4.5) * mm});
            skLineSegment(sketch, "E38.8.0.3", {"start": v(-44.24, 4.5) * mm, "end": v(-44.24, 5.75) * mm});
            skLineSegment(sketch, "E38.8.0.4", {"start": v(-45.04, 4.5) * mm, "end": v(-44.24, 4.5) * mm});
            skLineSegment(sketch, "E38.9.0.0", {"start": v(-40.67, 5.75) * mm, "end": v(-41.07, 5.75) * mm});
            skLineSegment(sketch, "E38.9.0.1", {"start": v(-41.07, 5.75) * mm, "end": v(-41.47, 5.75) * mm});
            skLineSegment(sketch, "E38.9.0.2", {"start": v(-41.47, 5.75) * mm, "end": v(-41.47, 4.5) * mm});
            skLineSegment(sketch, "E38.9.0.3", {"start": v(-40.67, 4.5) * mm, "end": v(-40.67, 5.75) * mm});
            skLineSegment(sketch, "E38.9.0.4", {"start": v(-41.47, 4.5) * mm, "end": v(-40.67, 4.5) * mm});
            skLineSegment(sketch, "E38.10.0.0", {"start": v(-37.1, 5.75) * mm, "end": v(-37.5, 5.75) * mm});
            skLineSegment(sketch, "E38.10.0.1", {"start": v(-37.5, 5.75) * mm, "end": v(-37.9, 5.75) * mm});
            skLineSegment(sketch, "E38.10.0.2", {"start": v(-37.9, 5.75) * mm, "end": v(-37.9, 4.5) * mm});
            skLineSegment(sketch, "E38.10.0.3", {"start": v(-37.1, 4.5) * mm, "end": v(-37.1, 5.75) * mm});
            skLineSegment(sketch, "E38.10.0.4", {"start": v(-37.9, 4.5) * mm, "end": v(-37.1, 4.5) * mm});
            skLineSegment(sketch, "E38.11.0.0", {"start": v(-33.53, 5.75) * mm, "end": v(-33.93, 5.75) * mm});
            skLineSegment(sketch, "E38.11.0.1", {"start": v(-33.93, 5.75) * mm, "end": v(-34.33, 5.75) * mm});
            skLineSegment(sketch, "E38.11.0.2", {"start": v(-34.33, 5.75) * mm, "end": v(-34.33, 4.5) * mm});
            skLineSegment(sketch, "E38.11.0.3", {"start": v(-33.53, 4.5) * mm, "end": v(-33.53, 5.75) * mm});
            skLineSegment(sketch, "E38.11.0.4", {"start": v(-34.33, 4.5) * mm, "end": v(-33.53, 4.5) * mm});
            skLineSegment(sketch, "E38.12.0.0", {"start": v(-29.96, 5.75) * mm, "end": v(-30.36, 5.75) * mm});
            skLineSegment(sketch, "E38.12.0.1", {"start": v(-30.36, 5.75) * mm, "end": v(-30.76, 5.75) * mm});
            skLineSegment(sketch, "E38.12.0.2", {"start": v(-30.76, 5.75) * mm, "end": v(-30.76, 4.5) * mm});
            skLineSegment(sketch, "E38.12.0.3", {"start": v(-29.96, 4.5) * mm, "end": v(-29.96, 5.75) * mm});
            skLineSegment(sketch, "E38.12.0.4", {"start": v(-30.76, 4.5) * mm, "end": v(-29.96, 4.5) * mm});
            skLineSegment(sketch, "E38.13.0.0", {"start": v(-26.39, 5.75) * mm, "end": v(-26.79, 5.75) * mm});
            skLineSegment(sketch, "E38.13.0.1", {"start": v(-26.79, 5.75) * mm, "end": v(-27.19, 5.75) * mm});
            skLineSegment(sketch, "E38.13.0.2", {"start": v(-27.19, 5.75) * mm, "end": v(-27.19, 4.5) * mm});
            skLineSegment(sketch, "E38.13.0.3", {"start": v(-26.39, 4.5) * mm, "end": v(-26.39, 5.75) * mm});
            skLineSegment(sketch, "E38.13.0.4", {"start": v(-27.19, 4.5) * mm, "end": v(-26.39, 4.5) * mm});
            skLineSegment(sketch, "E38.14.0.0", {"start": v(-22.82, 5.75) * mm, "end": v(-23.22, 5.75) * mm});
            skLineSegment(sketch, "E38.14.0.1", {"start": v(-23.22, 5.75) * mm, "end": v(-23.62, 5.75) * mm});
            skLineSegment(sketch, "E38.14.0.2", {"start": v(-23.62, 5.75) * mm, "end": v(-23.62, 4.5) * mm});
            skLineSegment(sketch, "E38.14.0.3", {"start": v(-22.82, 4.5) * mm, "end": v(-22.82, 5.75) * mm});
            skLineSegment(sketch, "E38.14.0.4", {"start": v(-23.62, 4.5) * mm, "end": v(-22.82, 4.5) * mm});
            skLineSegment(sketch, "E38.15.0.0", {"start": v(-19.25, 5.75) * mm, "end": v(-19.65, 5.75) * mm});
            skLineSegment(sketch, "E38.15.0.1", {"start": v(-19.65, 5.75) * mm, "end": v(-20.05, 5.75) * mm});
            skLineSegment(sketch, "E38.15.0.2", {"start": v(-20.05, 5.75) * mm, "end": v(-20.05, 4.5) * mm});
            skLineSegment(sketch, "E38.15.0.3", {"start": v(-19.25, 4.5) * mm, "end": v(-19.25, 5.75) * mm});
            skLineSegment(sketch, "E38.15.0.4", {"start": v(-20.05, 4.5) * mm, "end": v(-19.25, 4.5) * mm});
            skLineSegment(sketch, "E38.16.0.0", {"start": v(-15.68, 5.75) * mm, "end": v(-16.08, 5.75) * mm});
            skLineSegment(sketch, "E38.16.0.1", {"start": v(-16.08, 5.75) * mm, "end": v(-16.48, 5.75) * mm});
            skLineSegment(sketch, "E38.16.0.2", {"start": v(-16.48, 5.75) * mm, "end": v(-16.48, 4.5) * mm});
            skLineSegment(sketch, "E38.16.0.3", {"start": v(-15.68, 4.5) * mm, "end": v(-15.68, 5.75) * mm});
            skLineSegment(sketch, "E38.16.0.4", {"start": v(-16.48, 4.5) * mm, "end": v(-15.68, 4.5) * mm});
            skLineSegment(sketch, "E38.17.0.0", {"start": v(-12.1, 5.75) * mm, "end": v(-12.5, 5.75) * mm});
            skLineSegment(sketch, "E38.17.0.1", {"start": v(-12.5, 5.75) * mm, "end": v(-12.9, 5.75) * mm});
            skLineSegment(sketch, "E38.17.0.2", {"start": v(-12.9, 5.75) * mm, "end": v(-12.9, 4.5) * mm});
            skLineSegment(sketch, "E38.17.0.3", {"start": v(-12.1, 4.5) * mm, "end": v(-12.1, 5.75) * mm});
            skLineSegment(sketch, "E38.17.0.4", {"start": v(-12.9, 4.5) * mm, "end": v(-12.1, 4.5) * mm});
            skLineSegment(sketch, "E38.18.0.0", {"start": v(-8.54, 5.75) * mm, "end": v(-8.94, 5.75) * mm});
            skLineSegment(sketch, "E38.18.0.1", {"start": v(-8.94, 5.75) * mm, "end": v(-9.34, 5.75) * mm});
            skLineSegment(sketch, "E38.18.0.2", {"start": v(-9.34, 5.75) * mm, "end": v(-9.34, 4.5) * mm});
            skLineSegment(sketch, "E38.18.0.3", {"start": v(-8.54, 4.5) * mm, "end": v(-8.54, 5.75) * mm});
            skLineSegment(sketch, "E38.18.0.4", {"start": v(-9.34, 4.5) * mm, "end": v(-8.54, 4.5) * mm});
            skLineSegment(sketch, "E38.19.0.0", {"start": v(-4.97, 5.75) * mm, "end": v(-5.37, 5.75) * mm});
            skLineSegment(sketch, "E38.19.0.1", {"start": v(-5.37, 5.75) * mm, "end": v(-5.77, 5.75) * mm});
            skLineSegment(sketch, "E38.19.0.2", {"start": v(-5.77, 5.75) * mm, "end": v(-5.77, 4.5) * mm});
            skLineSegment(sketch, "E38.19.0.3", {"start": v(-4.97, 4.5) * mm, "end": v(-4.97, 5.75) * mm});
            skLineSegment(sketch, "E38.19.0.4", {"start": v(-5.77, 4.5) * mm, "end": v(-4.97, 4.5) * mm});
            skLineSegment(sketch, "E38.20.0.0", {"start": v(-1.4, 5.75) * mm, "end": v(-1.8, 5.75) * mm});
            skLineSegment(sketch, "E38.20.0.1", {"start": v(-1.8, 5.75) * mm, "end": v(-2.2, 5.75) * mm});
            skLineSegment(sketch, "E38.20.0.2", {"start": v(-2.2, 5.75) * mm, "end": v(-2.2, 4.5) * mm});
            skLineSegment(sketch, "E38.20.0.3", {"start": v(-1.4, 4.5) * mm, "end": v(-1.4, 5.75) * mm});
            skLineSegment(sketch, "E38.20.0.4", {"start": v(-2.2, 4.5) * mm, "end": v(-1.4, 4.5) * mm});
            skLineSegment(sketch, "E38.direction1", {"start": v(-73.2, 5.75) * mm, "end": v(-69.63, 5.75) * mm, "construction": true});
            skSolve(sketch);
        }
        {
            var Q0;
            Q0=qSketchRegion(id+"F8",true);
            extrude(context, id + "F9", {"entities" : qUnion([Q0]), "operationType" : NewBodyOperationType.ADD, "oppositeDirection" : true, "depth" : 2.25 * mm, "offsetDistance" : 25 * mm});
        }
        {
            var Q0;
            Q0=makeQuery(id+"F1.opExtrude","SWEPT_FACE",FACE,{"disambiguationData":[OSD([sQuery(id+"F0.wireOp",EDGE,"E7")])]});
            var sketch = newSketch(context, id + "F10", { "sketchPlane" : qUnion([Q0])});
            skLineSegment(sketch, "E39", {"start": v(1.75, 3.83) * mm, "end": v(1.75, 6.83) * mm, "construction": true});
            skLineSegment(sketch, "E40.bottom", {"start": v(0.53, 5.53) * mm, "end": v(2.96, 5.53) * mm});
            skLineSegment(sketch, "E40.top", {"start": v(0.53, 5.12) * mm, "end": v(2.96, 5.12) * mm});
            skLineSegment(sketch, "E40.left", {"start": v(0.53, 5.53) * mm, "end": v(0.53, 5.12) * mm});
            skLineSegment(sketch, "E40.right", {"start": v(2.96, 5.53) * mm, "end": v(2.96, 5.12) * mm});
            skPoint(sketch, "E40.middle", {"position": v(1.75, 5.33) * mm});
            skLineSegment(sketch, "E41.1.0.0", {"start": v(4.1, 5.12) * mm, "end": v(6.53, 5.12) * mm});
            skLineSegment(sketch, "E41.1.0.1", {"start": v(4.1, 5.53) * mm, "end": v(6.53, 5.53) * mm});
            skLineSegment(sketch, "E41.1.0.2", {"start": v(4.1, 5.53) * mm, "end": v(4.1, 5.12) * mm});
            skLineSegment(sketch, "E41.1.0.3", {"start": v(6.53, 5.53) * mm, "end": v(6.53, 5.12) * mm});
            skLineSegment(sketch, "E41.2.0.0", {"start": v(7.67, 5.12) * mm, "end": v(10.1, 5.12) * mm});
            skLineSegment(sketch, "E41.2.0.1", {"start": v(7.67, 5.53) * mm, "end": v(10.1, 5.53) * mm});
            skLineSegment(sketch, "E41.2.0.2", {"start": v(7.67, 5.53) * mm, "end": v(7.67, 5.12) * mm});
            skLineSegment(sketch, "E41.2.0.3", {"start": v(10.1, 5.53) * mm, "end": v(10.1, 5.12) * mm});
            skLineSegment(sketch, "E41.3.0.0", {"start": v(11.24, 5.12) * mm, "end": v(13.67, 5.12) * mm});
            skLineSegment(sketch, "E41.3.0.1", {"start": v(11.24, 5.53) * mm, "end": v(13.67, 5.53) * mm});
            skLineSegment(sketch, "E41.3.0.2", {"start": v(11.24, 5.53) * mm, "end": v(11.24, 5.12) * mm});
            skLineSegment(sketch, "E41.3.0.3", {"start": v(13.67, 5.53) * mm, "end": v(13.67, 5.12) * mm});
            skLineSegment(sketch, "E41.4.0.0", {"start": v(14.81, 5.12) * mm, "end": v(17.24, 5.12) * mm});
            skLineSegment(sketch, "E41.4.0.1", {"start": v(14.81, 5.53) * mm, "end": v(17.24, 5.53) * mm});
            skLineSegment(sketch, "E41.4.0.2", {"start": v(14.81, 5.53) * mm, "end": v(14.81, 5.12) * mm});
            skLineSegment(sketch, "E41.4.0.3", {"start": v(17.24, 5.53) * mm, "end": v(17.24, 5.12) * mm});
            skLineSegment(sketch, "E41.5.0.0", {"start": v(18.38, 5.12) * mm, "end": v(20.81, 5.12) * mm});
            skLineSegment(sketch, "E41.5.0.1", {"start": v(18.38, 5.53) * mm, "end": v(20.81, 5.53) * mm});
            skLineSegment(sketch, "E41.5.0.2", {"start": v(18.38, 5.53) * mm, "end": v(18.38, 5.12) * mm});
            skLineSegment(sketch, "E41.5.0.3", {"start": v(20.81, 5.53) * mm, "end": v(20.81, 5.12) * mm});
            skLineSegment(sketch, "E41.6.0.0", {"start": v(21.95, 5.12) * mm, "end": v(24.38, 5.12) * mm});
            skLineSegment(sketch, "E41.6.0.1", {"start": v(21.95, 5.53) * mm, "end": v(24.38, 5.53) * mm});
            skLineSegment(sketch, "E41.6.0.2", {"start": v(21.95, 5.53) * mm, "end": v(21.95, 5.12) * mm});
            skLineSegment(sketch, "E41.6.0.3", {"start": v(24.38, 5.53) * mm, "end": v(24.38, 5.12) * mm});
            skLineSegment(sketch, "E41.7.0.0", {"start": v(25.52, 5.12) * mm, "end": v(27.95, 5.12) * mm});
            skLineSegment(sketch, "E41.7.0.1", {"start": v(25.52, 5.53) * mm, "end": v(27.95, 5.53) * mm});
            skLineSegment(sketch, "E41.7.0.2", {"start": v(25.52, 5.53) * mm, "end": v(25.52, 5.12) * mm});
            skLineSegment(sketch, "E41.7.0.3", {"start": v(27.95, 5.53) * mm, "end": v(27.95, 5.12) * mm});
            skLineSegment(sketch, "E41.8.0.0", {"start": v(29.1, 5.12) * mm, "end": v(31.52, 5.12) * mm});
            skLineSegment(sketch, "E41.8.0.1", {"start": v(29.1, 5.53) * mm, "end": v(31.52, 5.53) * mm});
            skLineSegment(sketch, "E41.8.0.2", {"start": v(29.1, 5.53) * mm, "end": v(29.1, 5.12) * mm});
            skLineSegment(sketch, "E41.8.0.3", {"start": v(31.52, 5.53) * mm, "end": v(31.52, 5.12) * mm});
            skLineSegment(sketch, "E41.9.0.0", {"start": v(32.66, 5.12) * mm, "end": v(35.1, 5.12) * mm});
            skLineSegment(sketch, "E41.9.0.1", {"start": v(32.66, 5.53) * mm, "end": v(35.1, 5.53) * mm});
            skLineSegment(sketch, "E41.9.0.2", {"start": v(32.66, 5.53) * mm, "end": v(32.66, 5.12) * mm});
            skLineSegment(sketch, "E41.9.0.3", {"start": v(35.1, 5.53) * mm, "end": v(35.1, 5.12) * mm});
            skLineSegment(sketch, "E41.10.0.0", {"start": v(36.23, 5.12) * mm, "end": v(38.66, 5.12) * mm});
            skLineSegment(sketch, "E41.10.0.1", {"start": v(36.23, 5.53) * mm, "end": v(38.66, 5.53) * mm});
            skLineSegment(sketch, "E41.10.0.2", {"start": v(36.23, 5.53) * mm, "end": v(36.23, 5.12) * mm});
            skLineSegment(sketch, "E41.10.0.3", {"start": v(38.66, 5.53) * mm, "end": v(38.66, 5.12) * mm});
            skLineSegment(sketch, "E41.11.0.0", {"start": v(39.8, 5.12) * mm, "end": v(42.23, 5.12) * mm});
            skLineSegment(sketch, "E41.11.0.1", {"start": v(39.8, 5.53) * mm, "end": v(42.23, 5.53) * mm});
            skLineSegment(sketch, "E41.11.0.2", {"start": v(39.8, 5.53) * mm, "end": v(39.8, 5.12) * mm});
            skLineSegment(sketch, "E41.11.0.3", {"start": v(42.23, 5.53) * mm, "end": v(42.23, 5.12) * mm});
            skLineSegment(sketch, "E41.12.0.0", {"start": v(43.37, 5.12) * mm, "end": v(45.8, 5.12) * mm});
            skLineSegment(sketch, "E41.12.0.1", {"start": v(43.37, 5.53) * mm, "end": v(45.8, 5.53) * mm});
            skLineSegment(sketch, "E41.12.0.2", {"start": v(43.37, 5.53) * mm, "end": v(43.37, 5.12) * mm});
            skLineSegment(sketch, "E41.12.0.3", {"start": v(45.8, 5.53) * mm, "end": v(45.8, 5.12) * mm});
            skLineSegment(sketch, "E41.13.0.0", {"start": v(46.94, 5.12) * mm, "end": v(49.37, 5.12) * mm});
            skLineSegment(sketch, "E41.13.0.1", {"start": v(46.94, 5.53) * mm, "end": v(49.37, 5.53) * mm});
            skLineSegment(sketch, "E41.13.0.2", {"start": v(46.94, 5.53) * mm, "end": v(46.94, 5.12) * mm});
            skLineSegment(sketch, "E41.13.0.3", {"start": v(49.37, 5.53) * mm, "end": v(49.37, 5.12) * mm});
            skLineSegment(sketch, "E41.14.0.0", {"start": v(50.51, 5.12) * mm, "end": v(52.94, 5.12) * mm});
            skLineSegment(sketch, "E41.14.0.1", {"start": v(50.51, 5.53) * mm, "end": v(52.94, 5.53) * mm});
            skLineSegment(sketch, "E41.14.0.2", {"start": v(50.51, 5.53) * mm, "end": v(50.51, 5.12) * mm});
            skLineSegment(sketch, "E41.14.0.3", {"start": v(52.94, 5.53) * mm, "end": v(52.94, 5.12) * mm});
            skLineSegment(sketch, "E41.15.0.0", {"start": v(54.08, 5.12) * mm, "end": v(56.51, 5.12) * mm});
            skLineSegment(sketch, "E41.15.0.1", {"start": v(54.08, 5.53) * mm, "end": v(56.51, 5.53) * mm});
            skLineSegment(sketch, "E41.15.0.2", {"start": v(54.08, 5.53) * mm, "end": v(54.08, 5.12) * mm});
            skLineSegment(sketch, "E41.15.0.3", {"start": v(56.51, 5.53) * mm, "end": v(56.51, 5.12) * mm});
            skLineSegment(sketch, "E41.16.0.0", {"start": v(57.65, 5.12) * mm, "end": v(60.08, 5.12) * mm});
            skLineSegment(sketch, "E41.16.0.1", {"start": v(57.65, 5.53) * mm, "end": v(60.08, 5.53) * mm});
            skLineSegment(sketch, "E41.16.0.2", {"start": v(57.65, 5.53) * mm, "end": v(57.65, 5.12) * mm});
            skLineSegment(sketch, "E41.16.0.3", {"start": v(60.08, 5.53) * mm, "end": v(60.08, 5.12) * mm});
            skLineSegment(sketch, "E41.17.0.0", {"start": v(61.22, 5.12) * mm, "end": v(63.65, 5.12) * mm});
            skLineSegment(sketch, "E41.17.0.1", {"start": v(61.22, 5.53) * mm, "end": v(63.65, 5.53) * mm});
            skLineSegment(sketch, "E41.17.0.2", {"start": v(61.22, 5.53) * mm, "end": v(61.22, 5.12) * mm});
            skLineSegment(sketch, "E41.17.0.3", {"start": v(63.65, 5.53) * mm, "end": v(63.65, 5.12) * mm});
            skLineSegment(sketch, "E41.18.0.0", {"start": v(64.8, 5.12) * mm, "end": v(67.22, 5.12) * mm});
            skLineSegment(sketch, "E41.18.0.1", {"start": v(64.8, 5.53) * mm, "end": v(67.22, 5.53) * mm});
            skLineSegment(sketch, "E41.18.0.2", {"start": v(64.8, 5.53) * mm, "end": v(64.8, 5.12) * mm});
            skLineSegment(sketch, "E41.18.0.3", {"start": v(67.22, 5.53) * mm, "end": v(67.22, 5.12) * mm});
            skLineSegment(sketch, "E41.19.0.0", {"start": v(68.36, 5.12) * mm, "end": v(70.8, 5.12) * mm});
            skLineSegment(sketch, "E41.19.0.1", {"start": v(68.36, 5.53) * mm, "end": v(70.8, 5.53) * mm});
            skLineSegment(sketch, "E41.19.0.2", {"start": v(68.36, 5.53) * mm, "end": v(68.36, 5.12) * mm});
            skLineSegment(sketch, "E41.19.0.3", {"start": v(70.8, 5.53) * mm, "end": v(70.8, 5.12) * mm});
            skLineSegment(sketch, "E41.20.0.0", {"start": v(71.93, 5.12) * mm, "end": v(74.36, 5.12) * mm});
            skLineSegment(sketch, "E41.20.0.1", {"start": v(71.93, 5.53) * mm, "end": v(74.36, 5.53) * mm});
            skLineSegment(sketch, "E41.20.0.2", {"start": v(71.93, 5.53) * mm, "end": v(71.93, 5.12) * mm});
            skLineSegment(sketch, "E41.20.0.3", {"start": v(74.36, 5.53) * mm, "end": v(74.36, 5.12) * mm});
            skLineSegment(sketch, "E41.direction1", {"start": v(0.53, 5.12) * mm, "end": v(4.1, 5.12) * mm, "construction": true});
            skSolve(sketch);
        }
        {
            var Q0;
            Q0=qSketchRegion(id+"F10",true);
            extrude(context, id + "F11", {"entities" : qUnion([Q0]), "operationType" : NewBodyOperationType.REMOVE, "oppositeDirection" : true, "depth" : 5 * mm, "offsetDistance" : 25 * mm});
        }
    });
